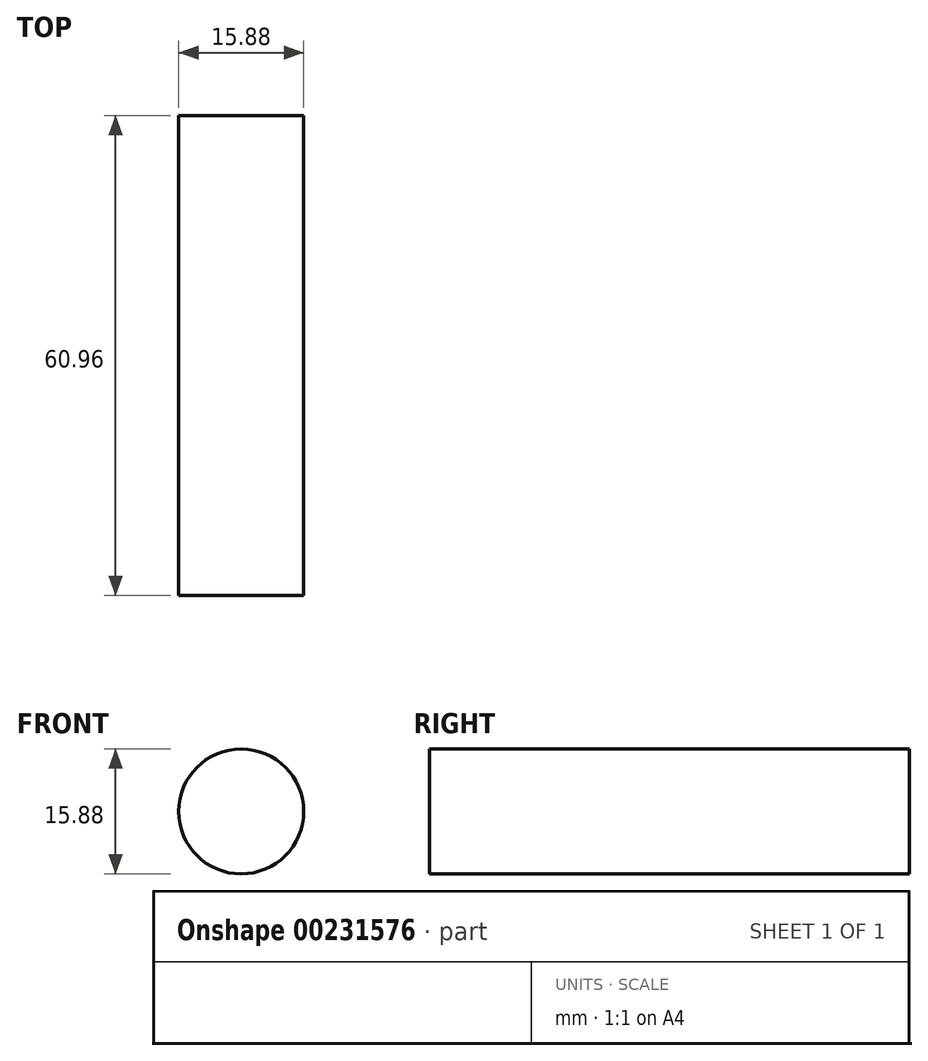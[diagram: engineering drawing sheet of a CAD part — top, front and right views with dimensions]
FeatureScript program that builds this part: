
annotation { "Feature Type Name" : "Feature", "Feature Type Description" : "" }
export const myFeature = defineFeature(function(context is Context, id is Id, definition is map)
    precondition{}
    {
        {
            var Q0;
            Q0=qCreatedBy(makeId("Front.planeOp"),FACE);
            var sketch = newSketch(context, id + "F0", { "sketchPlane" : qUnion([Q0])});
            skCircle(sketch, "E0", {"center": v(0, 0) * mm, "radius": 7.94 * mm});
            skSolve(sketch);
        }
        {
            var Q0;
            Q0 = qSketchRegion(id + "F0", true);
            extrude(context, id + "F1", {"entities" : qUnion([Q0]), "depth" : 60.96 * mm});
        }
    });
